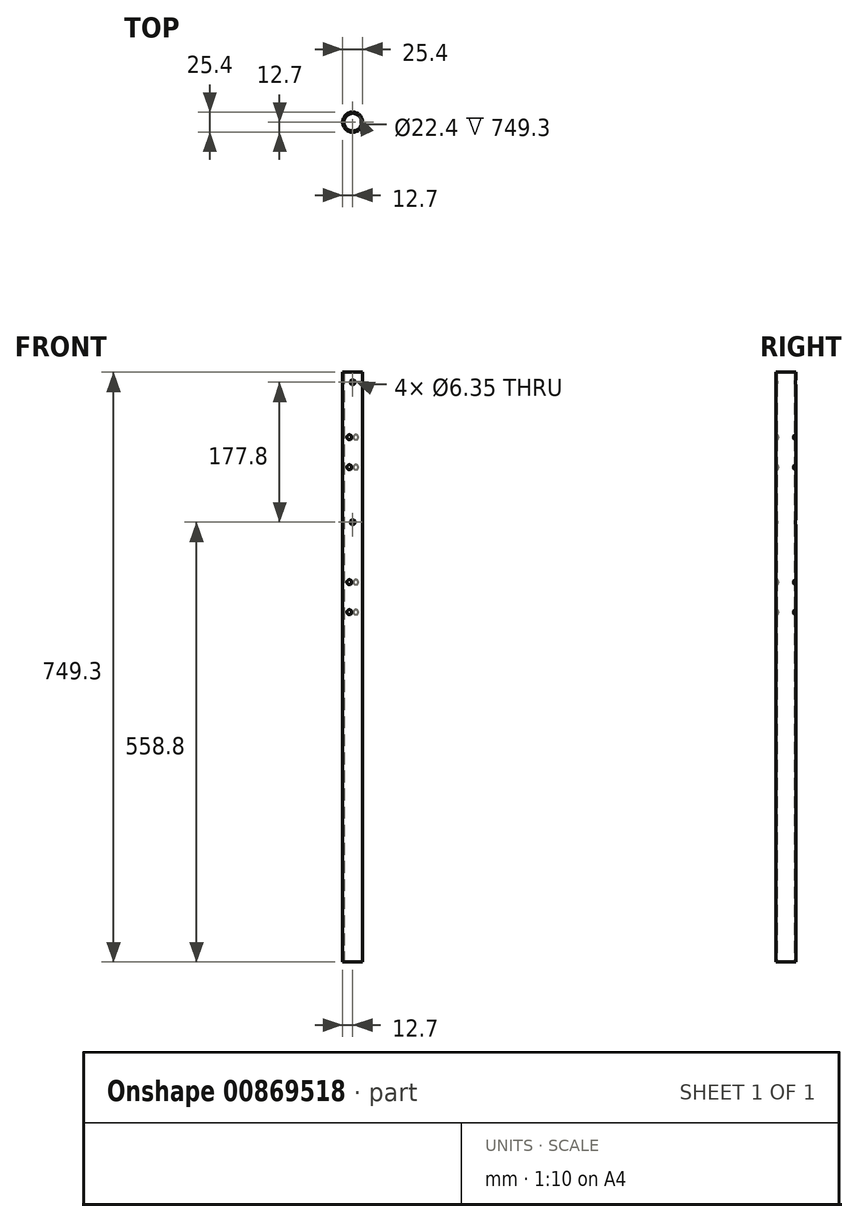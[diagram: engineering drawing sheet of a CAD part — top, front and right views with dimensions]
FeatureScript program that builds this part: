
annotation { "Feature Type Name" : "Feature", "Feature Type Description" : "" }
export const myFeature = defineFeature(function(context is Context, id is Id, definition is map)
    precondition{}
    {
        {
            var Q0;
            Q0=qCreatedBy(makeId("Top.planeOp"),FACE);
            var sketch = newSketch(context, id + "F0", { "sketchPlane" : qUnion([Q0])});
            skCircle(sketch, "E0", {"center": v(0, 0) * mm, "radius": 12.7 * mm});
            skCircle(sketch, "E1.0", {"center": v(0, 0) * mm, "radius": 11.2 * mm});
            skSolve(sketch);
        }
        {
            var Q0;
            Q0=makeQuery(id+"F0.imprint","IMPRINT",FACE,{"disambiguationData":[TD([[makeQuery(id+"F0.imprint","IMPRINT",EDGE,{"derivedFrom":sQuery(id+"F0.wireOp",EDGE,"E0")}),1.0]])]});
            extrude(context, id + "F1", {"entities" : qUnion([Q0]), "depth" : 749.3 * mm, "offsetDistance" : 25.4 * mm});
        }
        {
            var Q0;
            Q0=qCreatedBy(makeId("Front.planeOp"),FACE);
            var sketch = newSketch(context, id + "F2", { "sketchPlane" : qUnion([Q0])});
            skLineSegment(sketch, "E2", {"start": v(0, 0) * mm, "end": v(0, 749.3) * mm, "construction": true});
            skCircle(sketch, "E3", {"center": v(0, 558.8) * mm, "radius": 3.18 * mm});
            skCircle(sketch, "E4", {"center": v(0, 736.6) * mm, "radius": 3.18 * mm});
            skSolve(sketch);
        }
        {
            var Q0;
            Q0=qSketchRegion(id+"F2",true);
            extrude(context, id + "F3", {"entities" : qUnion([Q0]), "operationType" : NewBodyOperationType.REMOVE, "endBound" : BoundingType.SYMMETRIC, "depth" : 25.4 * mm, "offsetDistance" : 25.4 * mm});
        }
        {
            var Q0;
            Q0=qCreatedBy(makeId("Front.planeOp"),FACE);
            var sketch = newSketch(context, id + "F4", { "sketchPlane" : qUnion([Q0])});
            skLineSegment(sketch, "E5", {"start": v(0, 0) * mm, "end": v(0, 781.06) * mm});
            skSolve(sketch);
        }
        {
            var Q0;
            Q0=sQuery(id+"F4.wireOp",EDGE,"E5");
            cPlane(context, id + "F5", {"entities" : qUnion([Q0]), "cplaneType" : CPlaneType.LINE_ANGLE, "offset" : 25.4 * mm, "angle" : 290 * degree, "oppositeDirection" : true, "width" : 152.4 * mm, "height" : 152.4 * mm});
        }
        {
            var Q0;
            Q0=qCreatedBy(id+"F5.planeOp",FACE);
            var sketch = newSketch(context, id + "F6", { "sketchPlane" : qUnion([Q0])});
            skCircle(sketch, "E6", {"center": v(0, 628.65) * mm, "radius": 3.18 * mm});
            skCircle(sketch, "E7", {"center": v(0, 666.75) * mm, "radius": 3.18 * mm});
            skCircle(sketch, "E8", {"center": v(0, 444.5) * mm, "radius": 3.18 * mm});
            skCircle(sketch, "E9", {"center": v(0, 482.6) * mm, "radius": 3.18 * mm});
            skSolve(sketch);
        }
        {
            var Q0;
            Q0=qSketchRegion(id+"F6",true);
            extrude(context, id + "F7", {"entities" : qUnion([Q0]), "operationType" : NewBodyOperationType.REMOVE, "endBound" : BoundingType.SYMMETRIC, "oppositeDirection" : true, "depth" : 25.4 * mm, "offsetDistance" : 25.4 * mm});
        }
    });
